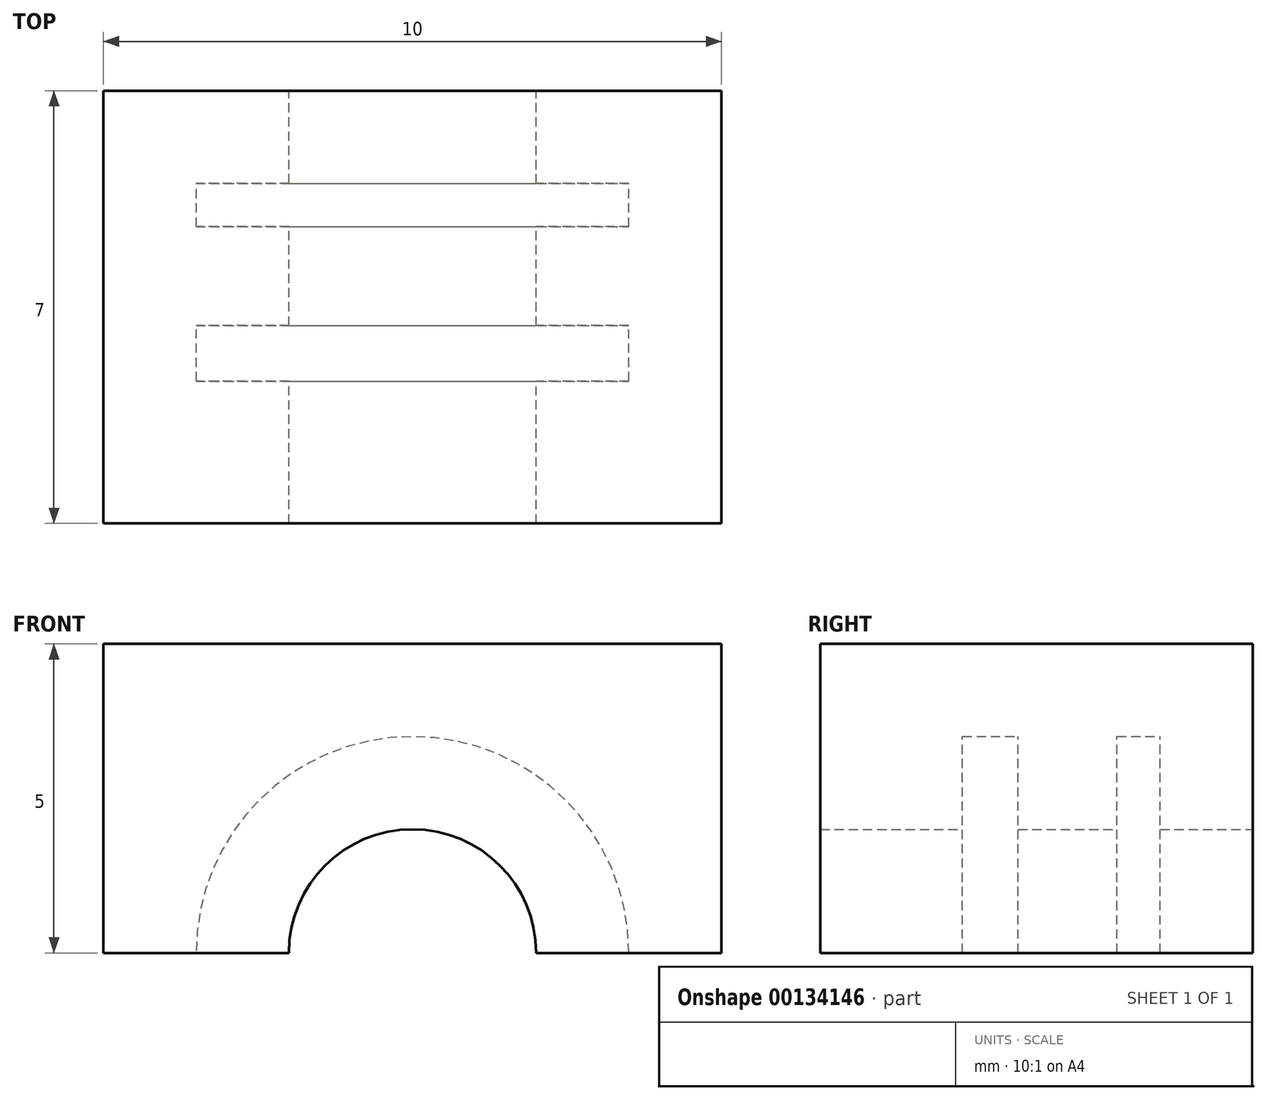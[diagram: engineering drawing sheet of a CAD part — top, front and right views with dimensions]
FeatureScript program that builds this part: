
annotation { "Feature Type Name" : "Feature", "Feature Type Description" : "" }
export const myFeature = defineFeature(function(context is Context, id is Id, definition is map)
    precondition{}
    {
        {
            var Q0;
            Q0=qCreatedBy(makeId("Top.planeOp"),FACE);
            var sketch = newSketch(context, id + "F0", { "sketchPlane" : qUnion([Q0])});
            skLineSegment(sketch, "E0.bottom", {"start": v(5, 3.5) * mm, "end": v(-5, 3.5) * mm});
            skLineSegment(sketch, "E0.top", {"start": v(5, -3.5) * mm, "end": v(-5, -3.5) * mm});
            skLineSegment(sketch, "E0.left", {"start": v(5, 3.5) * mm, "end": v(5, -3.5) * mm});
            skLineSegment(sketch, "E0.right", {"start": v(-5, 3.5) * mm, "end": v(-5, -3.5) * mm});
            skPoint(sketch, "E0.middle", {"position": v(0, 0) * mm});
            skSolve(sketch);
        }
        {
            var Q0;
            Q0=makeQuery(id+"F0.imprint","IMPRINT",FACE,{"disambiguationData":[TD([[makeQuery(id+"F0.imprint","IMPRINT",EDGE,{"derivedFrom":sQuery(id+"F0.wireOp",EDGE,"E0.bottom")}),1.0]])]});
            extrude(context, id + "F1", {"entities" : qUnion([Q0]), "depth" : 5 * mm});
        }
        {
            var Q0;
            Q0=makeQuery(id+"F1.opExtrude","SWEPT_FACE",FACE,{"disambiguationData":[OSD([sQuery(id+"F0.wireOp",EDGE,"E0.bottom")])]});
            var sketch = newSketch(context, id + "F2", { "sketchPlane" : qUnion([Q0])});
            skCircle(sketch, "E1", {"center": v(0, 0) * mm, "radius": 2 * mm});
            skSolve(sketch);
        }
        {
            var Q0;
            {var subQ0=sQuery(id+"F2.wireOp",EDGE,"E1");var subQ1=makeQuery(id+"F1.opExtrude","CAP_EDGE",EDGE,{"disambiguationData":[OSD([sQuery(id+"F0.wireOp",EDGE,"E0.bottom")])],"isStart":true});var subQ2=makeQuery(id+"F2.imprint","INTERSECT",VERTEX,{"disambiguationData":[OD(0.0)],"derivedFrom":[subQ1,subQ0]});Q0=makeQuery(id+"F2.imprint","IMPRINT",FACE,{"disambiguationData":[TD([[makeQuery(id+"F2.imprint","IMPRINT",EDGE,{"disambiguationData":[TD([[subQ2,1.0]])],"derivedFrom":subQ0}),1.0]])]});}
            extrude(context, id + "F3", {"entities" : qUnion([Q0]), "operationType" : NewBodyOperationType.REMOVE, "endBound" : BoundingType.UP_TO_NEXT, "oppositeDirection" : true, "depth" : 25 * mm});
        }
        {
            var Q0;
            Q0=makeQuery(id+"F1.opExtrude","SWEPT_FACE",FACE,{"disambiguationData":[OSD([sQuery(id+"F0.wireOp",EDGE,"E0.bottom")])]});
            cPlane(context, id + "F4", {"entities" : qUnion([Q0]), "cplaneType" : CPlaneType.OFFSET, "offset" : 1.5 * mm, "oppositeDirection" : true, "width" : 150 * mm, "height" : 150 * mm});
        }
        {
            var Q0;
            Q0=qCreatedBy(id+"F4.planeOp",FACE);
            var sketch = newSketch(context, id + "F5", { "sketchPlane" : qUnion([Q0])});
            skCircle(sketch, "E2", {"center": v(0, 0) * mm, "radius": 3.5 * mm});
            skSolve(sketch);
        }
        {
            var Q0;
            Q0=makeQuery(id+"F5.imprint","IMPRINT",FACE,{"disambiguationData":[TD([[makeQuery(id+"F5.imprint","IMPRINT",EDGE,{"derivedFrom":sQuery(id+"F5.wireOp",EDGE,"E2")}),1.0]])]});
            extrude(context, id + "F6", {"entities" : qUnion([Q0]), "operationType" : NewBodyOperationType.REMOVE, "oppositeDirection" : true, "depth" : 0.7 * mm});
        }
        {
            var Q0;
            Q0=makeQuery(id+"F6.boolean.opBoolean","COPY",FACE,{"derivedFrom":makeQuery(id+"F6.opExtrude","CAP_FACE",FACE,{"disambiguationData":[OSD([sQuery(id+"F5.wireOp",EDGE,"E2")])],"isStart":false})});
            cPlane(context, id + "F7", {"entities" : qUnion([Q0]), "cplaneType" : CPlaneType.OFFSET, "offset" : 1.6 * mm, "oppositeDirection" : true, "width" : 150 * mm, "height" : 150 * mm});
        }
        {
            var Q0;
            Q0=qCreatedBy(id+"F7.planeOp",FACE);
            var sketch = newSketch(context, id + "F8", { "sketchPlane" : qUnion([Q0])});
            skCircle(sketch, "E3", {"center": v(0, 0) * mm, "radius": 3.5 * mm});
            skSolve(sketch);
        }
        {
            var Q0;
            Q0=makeQuery(id+"F8.imprint","IMPRINT",FACE,{"disambiguationData":[TD([[makeQuery(id+"F8.imprint","IMPRINT",EDGE,{"derivedFrom":sQuery(id+"F8.wireOp",EDGE,"E3")}),1.0]])]});
            extrude(context, id + "F9", {"entities" : qUnion([Q0]), "operationType" : NewBodyOperationType.REMOVE, "oppositeDirection" : true, "depth" : 0.9 * mm});
        }
    });
